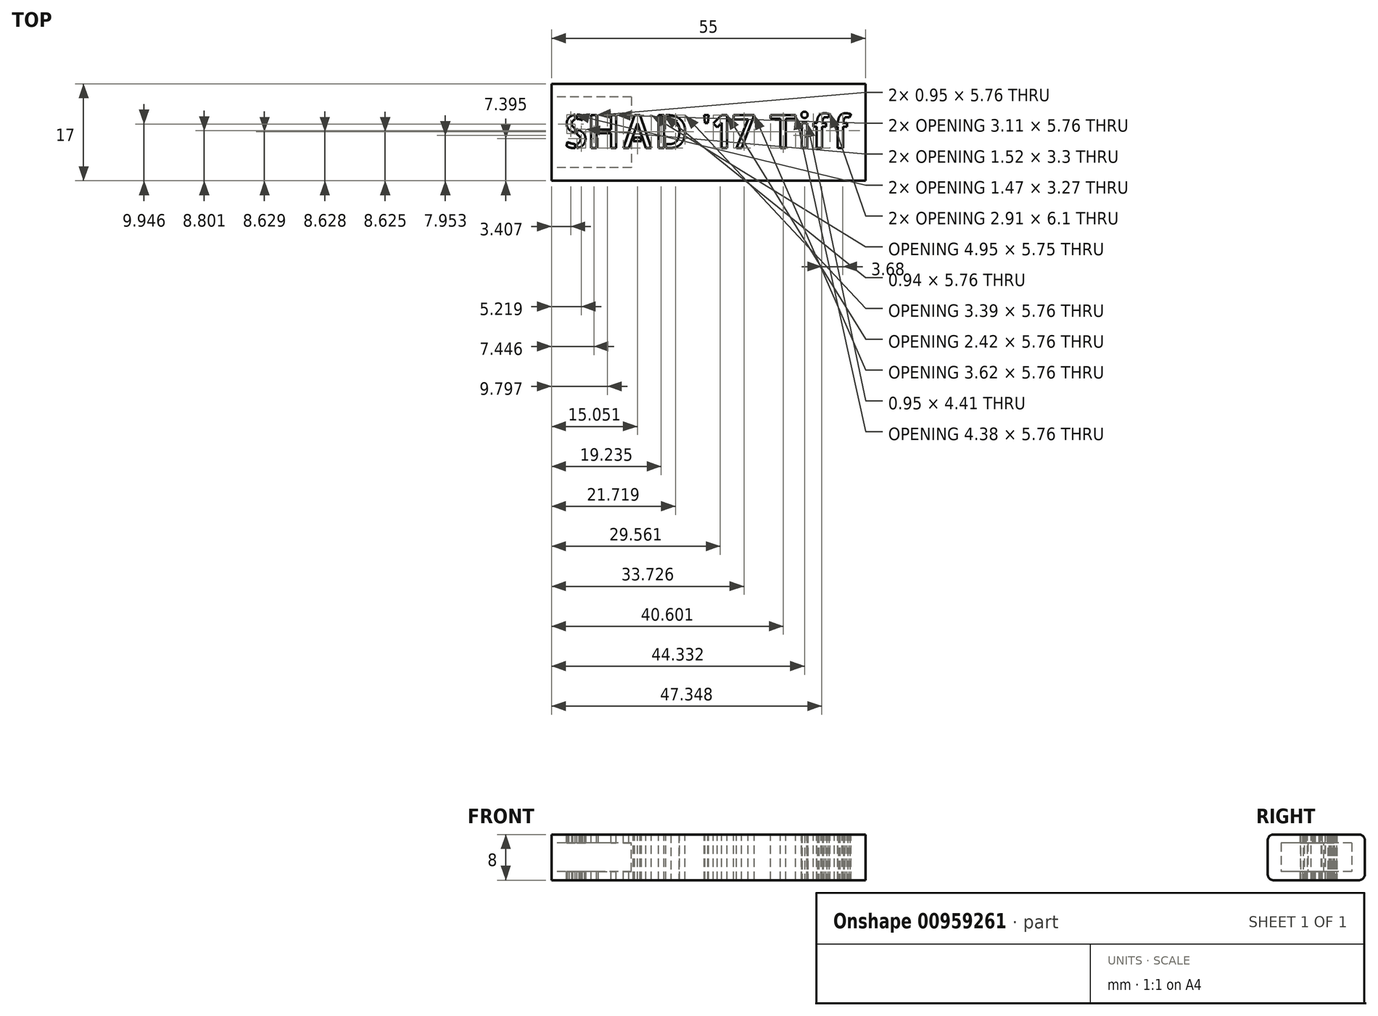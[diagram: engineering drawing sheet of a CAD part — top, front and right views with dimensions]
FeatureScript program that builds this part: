
annotation { "Feature Type Name" : "Feature", "Feature Type Description" : "" }
export const myFeature = defineFeature(function(context is Context, id is Id, definition is map)
    precondition{}
    {
        {
            var Q0;
            Q0=qCreatedBy(makeId("Front.planeOp"),FACE);
            var sketch = newSketch(context, id + "F0", { "sketchPlane" : qUnion([Q0])});
            skLineSegment(sketch, "E0.bottom", {"start": v(7.5, 4) * mm, "end": v(-7.5, 4) * mm});
            skLineSegment(sketch, "E0.top", {"start": v(7.5, -4) * mm, "end": v(-7.5, -4) * mm});
            skLineSegment(sketch, "E0.left", {"start": v(8.5, 3) * mm, "end": v(8.5, -3) * mm});
            skLineSegment(sketch, "E0.right", {"start": v(-8.5, 3) * mm, "end": v(-8.5, -3) * mm});
            skPoint(sketch, "E0.middle", {"position": v(0, 0) * mm});
            skPoint(sketch, "E1.visualSharp", {"position": v(-8.5, 4) * mm});
            skArc(sketch, "E1.filletArc", {"start": v(-7.5, 4) * mm, "mid": v(-8.2, 3.7) * mm, "end": v(-8.5, 3) * mm});
            skPoint(sketch, "E2.visualSharp", {"position": v(-8.5, -4) * mm});
            skArc(sketch, "E2.filletArc", {"start": v(-8.5, -3) * mm, "mid": v(-8.2, -3.7) * mm, "end": v(-7.5, -4) * mm});
            skPoint(sketch, "E3.visualSharp", {"position": v(8.5, -4) * mm});
            skArc(sketch, "E3.filletArc", {"start": v(7.5, -4) * mm, "mid": v(8.2, -3.7) * mm, "end": v(8.5, -3) * mm});
            skPoint(sketch, "E4.visualSharp", {"position": v(8.5, 4) * mm});
            skArc(sketch, "E4.filletArc", {"start": v(8.5, 3) * mm, "mid": v(8.2, 3.7) * mm, "end": v(7.5, 4) * mm});
            skSolve(sketch);
        }
        {
            var Q0;
            Q0=makeQuery(id+"F0.imprint","IMPRINT",FACE,{"disambiguationData":[TD([[makeQuery(id+"F0.imprint","IMPRINT",EDGE,{"derivedFrom":sQuery(id+"F0.wireOp",EDGE,"E0.bottom")}),1.0]])]});
            extrude(context, id + "F1", {"entities" : qUnion([Q0]), "endBound" : BoundingType.SYMMETRIC, "depth" : 55 * mm, "offsetDistance" : 25 * mm});
        }
        {
            var Q0;
            Q0=makeQuery(id+"F1.opExtrude","CAP_FACE",FACE,{"disambiguationData":[OSD([sQuery(id+"F0.wireOp",EDGE,"E0.bottom"),sQuery(id+"F0.wireOp",EDGE,"E0.top"),sQuery(id+"F0.wireOp",EDGE,"E0.left"),sQuery(id+"F0.wireOp",EDGE,"E0.right"),sQuery(id+"F0.wireOp",EDGE,"E1.filletArc"),sQuery(id+"F0.wireOp",EDGE,"E2.filletArc"),sQuery(id+"F0.wireOp",EDGE,"E3.filletArc"),sQuery(id+"F0.wireOp",EDGE,"E4.filletArc")])],"isStart":false});
            var sketch = newSketch(context, id + "F2", { "sketchPlane" : qUnion([Q0])});
            skLineSegment(sketch, "E5.bottom", {"start": v(-6.2, 2.5) * mm, "end": v(6.2, 2.5) * mm});
            skLineSegment(sketch, "E5.top", {"start": v(-6.2, -2.5) * mm, "end": v(6.2, -2.5) * mm});
            skLineSegment(sketch, "E5.left", {"start": v(-6.2, 2.5) * mm, "end": v(-6.2, -2.5) * mm});
            skLineSegment(sketch, "E5.right", {"start": v(6.2, 2.5) * mm, "end": v(6.2, -2.5) * mm});
            skSolve(sketch);
        }
        {
            var Q0;
            Q0 = qSketchRegion(id + "F2", true);
            extrude(context, id + "F3", {"entities" : qUnion([Q0]), "operationType" : NewBodyOperationType.REMOVE, "oppositeDirection" : true, "depth" : 14 * mm, "offsetDistance" : 25 * mm});
        }
        {
            var Q0;
            Q0=makeQuery(id+"F1.opExtrude","SWEPT_BODY",BODY,{"disambiguationData":[OSD([sQuery(id+"F0.wireOp",EDGE,"E0.bottom"),sQuery(id+"F0.wireOp",EDGE,"E0.top"),sQuery(id+"F0.wireOp",EDGE,"E0.left"),sQuery(id+"F0.wireOp",EDGE,"E0.right"),sQuery(id+"F0.wireOp",EDGE,"E1.filletArc"),sQuery(id+"F0.wireOp",EDGE,"E2.filletArc"),sQuery(id+"F0.wireOp",EDGE,"E3.filletArc"),sQuery(id+"F0.wireOp",EDGE,"E4.filletArc")])]});
            var Q1;
            Q1=makeQuery(id+"F1.opExtrude","CAP_EDGE",EDGE,{"disambiguationData":[OSD([sQuery(id+"F0.wireOp",EDGE,"E0.right")])],"isStart":true});
            transform(context, id + "F4", {"entities" : qUnion([Q0]), "transformType" : TransformType.ROTATION, "transformAxis" : qUnion([Q1]), "angle" : 90 * degree, "makeCopy" : false});
        }
        {
            var Q0;
            Q0=makeQuery(id+"F1.opExtrude","SWEPT_BODY",BODY,{"disambiguationData":[OSD([sQuery(id+"F0.wireOp",EDGE,"E0.bottom"),sQuery(id+"F0.wireOp",EDGE,"E0.top"),sQuery(id+"F0.wireOp",EDGE,"E0.left"),sQuery(id+"F0.wireOp",EDGE,"E0.right"),sQuery(id+"F0.wireOp",EDGE,"E1.filletArc"),sQuery(id+"F0.wireOp",EDGE,"E2.filletArc"),sQuery(id+"F0.wireOp",EDGE,"E3.filletArc"),sQuery(id+"F0.wireOp",EDGE,"E4.filletArc")])]});
            transform(context, id + "F5", {"entities" : qUnion([Q0]), "transformType" : TransformType.TRANSLATION_3D, "dx" : 36 * mm, "dy" : -19 * mm, "dz" : 0 * mm, "makeCopy" : false});
        }
        {
            var Q0;
            Q0=makeQuery(id+"F1.opExtrude","SWEPT_FACE",FACE,{"disambiguationData":[OSD([sQuery(id+"F0.wireOp",EDGE,"E0.bottom")])]});
            var sketch = newSketch(context, id + "F6", { "sketchPlane" : qUnion([Q0])});
            skText(sketch, "E6", { "text": "SHAD \'17 Tiff", "fontName": "AllertaStencil-Regular.ttf"});
            const initialGuessF6  = {"E6": [-0.0255, -0.00275, 1, 0, 0.00576]};
            skSetInitialGuess(sketch, initialGuessF6);
            skSolve(sketch);
        }
        {
            var Q0;
            Q0 = qSketchRegion(id + "F6", true);
            extrude(context, id + "F7", {"entities" : qUnion([Q0]), "operationType" : NewBodyOperationType.REMOVE, "oppositeDirection" : true, "depth" : 10 * mm, "offsetDistance" : 25 * mm});
        }
    });
